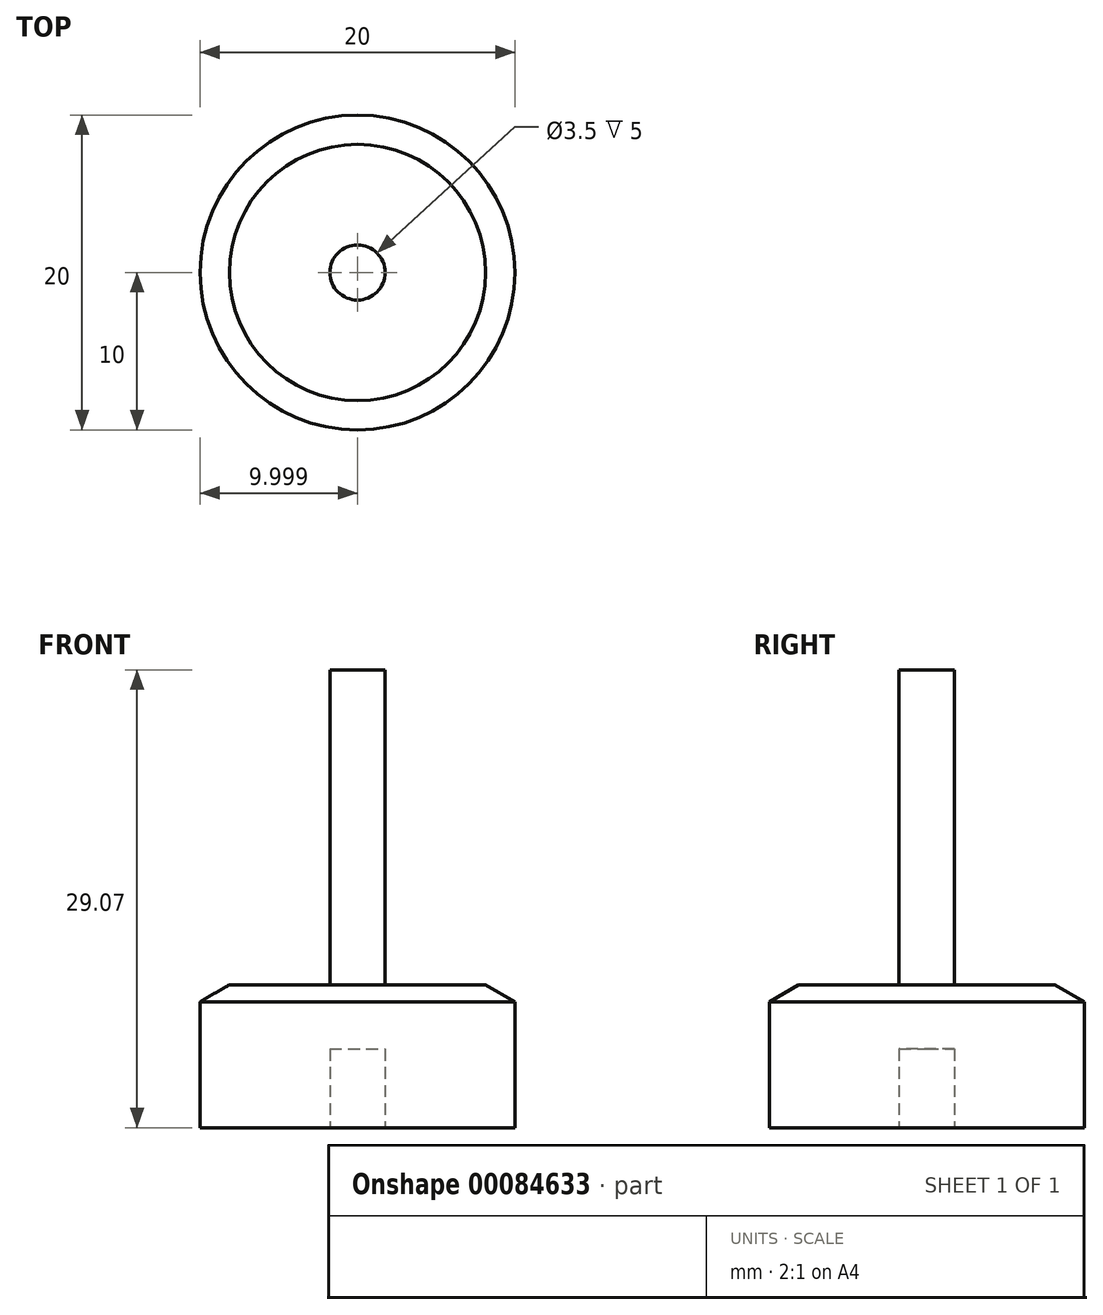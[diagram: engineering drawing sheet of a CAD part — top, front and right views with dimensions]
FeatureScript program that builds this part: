
annotation { "Feature Type Name" : "Feature", "Feature Type Description" : "" }
export const myFeature = defineFeature(function(context is Context, id is Id, definition is map)
    precondition{}
    {
        {
            var Q0;
            Q0=qCreatedBy(makeId("Front.planeOp"),FACE);
            var sketch = newSketch(context, id + "F0", { "sketchPlane" : qUnion([Q0])});
            skLineSegment(sketch, "E0.bottom", {"start": v(-30.55, 8) * mm, "end": v(-20.55, 8) * mm});
            skLineSegment(sketch, "E0.top", {"start": v(-30.55, 0) * mm, "end": v(-22.3, 0) * mm});
            skLineSegment(sketch, "E0.left", {"start": v(-30.55, 8) * mm, "end": v(-30.55, 0) * mm});
            skPoint(sketch, "E1", {"position": v(-20.55, 8) * mm});
            skPoint(sketch, "E2", {"position": v(-20.55, 0) * mm});
            skPoint(sketch, "E3", {"position": v(-20.55, 9.07) * mm});
            skLineSegment(sketch, "E4", {"start": v(-20.55, 8) * mm, "end": v(-20.55, 9.07) * mm});
            skLineSegment(sketch, "E5", {"start": v(-30.55, 8) * mm, "end": v(-28.7, 9.07) * mm});
            skLineSegment(sketch, "E6", {"start": v(-28.7, 9.07) * mm, "end": v(-20.55, 9.07) * mm});
            skLineSegment(sketch, "E7", {"start": v(-20.55, 8) * mm, "end": v(-20.55, 5) * mm});
            skPoint(sketch, "E0.right.end.orphan", {"position": v(-10.55, 0) * mm});
            skPoint(sketch, "E8.start.orphan", {"position": v(-10.55, 8) * mm});
            skLineSegment(sketch, "E9", {"start": v(-20.55, 9.07) * mm, "end": v(-20.55, 29.07) * mm});
            skLineSegment(sketch, "E10", {"start": v(-20.55, 29.07) * mm, "end": v(-22.3, 29.07) * mm});
            skLineSegment(sketch, "E11", {"start": v(-22.3, 29.07) * mm, "end": v(-22.3, 0) * mm});
            skPoint(sketch, "E12.start.orphan", {"position": v(-20.55, 4) * mm});
            skLineSegment(sketch, "E13", {"start": v(-20.55, 5) * mm, "end": v(-22.3, 5) * mm});
            skPoint(sketch, "E14", {"position": v(-20.55, 5) * mm});
            skSolve(sketch);
        }
        {
            var Q0;
            {var subQ0=sQuery(id+"F0.wireOp",EDGE,"E9");Q0=makeQuery(id+"F0.imprint","IMPRINT",FACE,{"disambiguationData":[TD([[makeQuery(id+"F0.imprint","IMPRINT",EDGE,{"derivedFrom":subQ0}),1.0]])]});}
            var Q1;
            {var subQ5=sQuery(id+"F0.wireOp",EDGE,"E0.top");Q1=makeQuery(id+"F0.imprint","IMPRINT",FACE,{"disambiguationData":[TD([[makeQuery(id+"F0.imprint","IMPRINT",EDGE,{"derivedFrom":subQ5}),1.0]])]});}
            var Q2;
            {var subQ0=sQuery(id+"F0.wireOp",EDGE,"E5");Q2=makeQuery(id+"F0.imprint","IMPRINT",FACE,{"disambiguationData":[TD([[makeQuery(id+"F0.imprint","IMPRINT",EDGE,{"derivedFrom":subQ0}),-1.0]])]});}
            var Q3;
            {var subQ0=sQuery(id+"F0.wireOp",EDGE,"E7");Q3=makeQuery(id+"F0.imprint","IMPRINT",FACE,{"disambiguationData":[TD([[makeQuery(id+"F0.imprint","IMPRINT",EDGE,{"derivedFrom":subQ0}),-1.0]])]});}
            var Q4;
            {var subQ0=sQuery(id+"F0.wireOp",EDGE,"E4");Q4=makeQuery(id+"F0.imprint","IMPRINT",FACE,{"disambiguationData":[TD([[makeQuery(id+"F0.imprint","IMPRINT",EDGE,{"derivedFrom":subQ0}),1.0]])]});}
            var Q5;
            Q5=sQuery(id+"F0.wireOp",EDGE,"E9");
            revolve(context, id + "F1", {"entities" : qUnion([Q0, Q1, Q2, Q3, Q4]), "axis" : qUnion([Q5]), "revolveType" : RevolveType.FULL});
        }
    });
